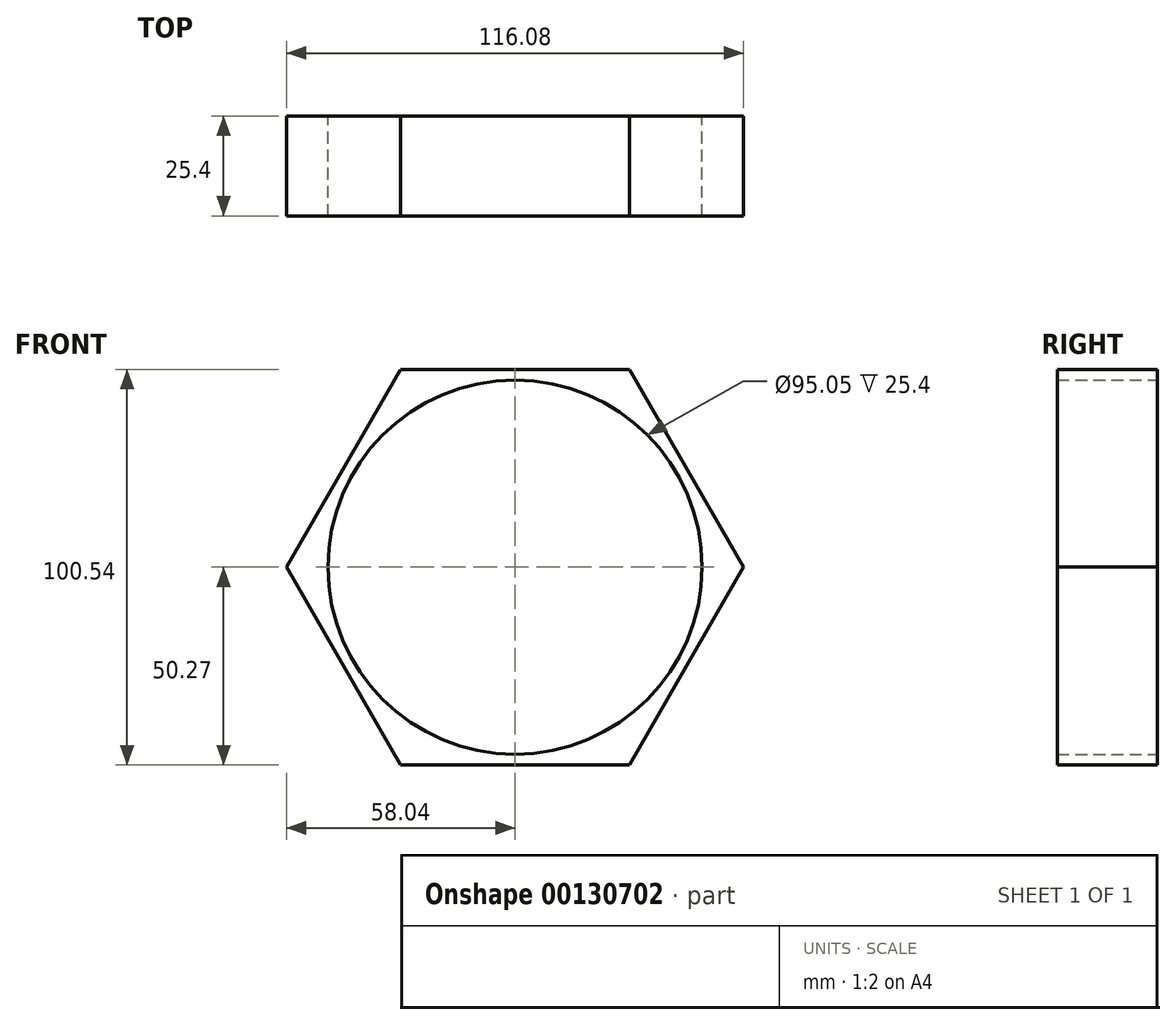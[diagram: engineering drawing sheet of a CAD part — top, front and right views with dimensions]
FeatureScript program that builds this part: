
annotation { "Feature Type Name" : "Feature", "Feature Type Description" : "" }
export const myFeature = defineFeature(function(context is Context, id is Id, definition is map)
    precondition{}
    {
        {
            var Q0;
            Q0=qCreatedBy(makeId("Front.planeOp"),FACE);
            var sketch = newSketch(context, id + "F0", { "sketchPlane" : qUnion([Q0])});
            skCircle(sketch, "E0.cCircle", {"center": v(0, 0) * mm, "radius": 50.27 * mm, "construction": true});
            skLineSegment(sketch, "E0.0", {"start": v(-29.02, 50.27) * mm, "end": v(29.02, 50.27) * mm});
            skLineSegment(sketch, "E0.1", {"start": v(29.02, 50.27) * mm, "end": v(58.04, 0) * mm});
            skLineSegment(sketch, "E0.2", {"start": v(58.04, 0) * mm, "end": v(29.02, -50.27) * mm});
            skLineSegment(sketch, "E0.3", {"start": v(29.02, -50.27) * mm, "end": v(-29.02, -50.27) * mm});
            skLineSegment(sketch, "E0.4", {"start": v(-29.02, -50.27) * mm, "end": v(-58.04, 0) * mm});
            skLineSegment(sketch, "E0.5", {"start": v(-58.04, 0) * mm, "end": v(-29.02, 50.27) * mm});
            skPoint(sketch, "E0.0.midPoint", {"position": v(0, 50.27) * mm});
            skSolve(sketch);
        }
        {
            var Q0;
            Q0=makeQuery(id+"F0.imprint","IMPRINT",FACE,{"disambiguationData":[TD([[makeQuery(id+"F0.imprint","IMPRINT",EDGE,{"derivedFrom":sQuery(id+"F0.wireOp",EDGE,"E0.0")}),-1.0]])]});
            extrude(context, id + "F1", {"entities" : qUnion([Q0]), "depth" : 25.4 * mm});
        }
        {
            var Q0;
            Q0=makeQuery(id+"F1.opExtrude","CAP_FACE",FACE,{"disambiguationData":[OSD([sQuery(id+"F0.wireOp",EDGE,"E0.0"),sQuery(id+"F0.wireOp",EDGE,"E0.1"),sQuery(id+"F0.wireOp",EDGE,"E0.2"),sQuery(id+"F0.wireOp",EDGE,"E0.3"),sQuery(id+"F0.wireOp",EDGE,"E0.4"),sQuery(id+"F0.wireOp",EDGE,"E0.5")])],"isStart":true});
            var sketch = newSketch(context, id + "F2", { "sketchPlane" : qUnion([Q0])});
            skCircle(sketch, "E1", {"center": v(0, 0) * mm, "radius": 48.43 * mm});
            skSolve(sketch);
        }
        {
            var Q0;
            Q0=makeQuery(id+"F2.imprint","IMPRINT",FACE,{"disambiguationData":[TD([[makeQuery(id+"F2.imprint","IMPRINT",EDGE,{"derivedFrom":sQuery(id+"F2.wireOp",EDGE,"E1")}),1.0]])]});
            extrude(context, id + "F3", {"entities" : qUnion([Q0]), "operationType" : NewBodyOperationType.ADD, "oppositeDirection" : true, "depth" : 1.19 * mm});
        }
        {
            var Q0;
            Q0=makeQuery(id+"F1.opExtrude","CAP_FACE",FACE,{"disambiguationData":[OSD([sQuery(id+"F0.wireOp",EDGE,"E0.0"),sQuery(id+"F0.wireOp",EDGE,"E0.1"),sQuery(id+"F0.wireOp",EDGE,"E0.2"),sQuery(id+"F0.wireOp",EDGE,"E0.3"),sQuery(id+"F0.wireOp",EDGE,"E0.4"),sQuery(id+"F0.wireOp",EDGE,"E0.5")])],"isStart":true});
            var sketch = newSketch(context, id + "F4", { "sketchPlane" : qUnion([Q0])});
            skCircle(sketch, "E2", {"center": v(0, 0) * mm, "radius": 47.53 * mm});
            skSolve(sketch);
        }
        {
            var Q0;
            Q0=makeQuery(id+"F4.imprint","IMPRINT",FACE,{"disambiguationData":[TD([[makeQuery(id+"F4.imprint","IMPRINT",EDGE,{"derivedFrom":sQuery(id+"F4.wireOp",EDGE,"E2")}),1.0]])]});
            extrude(context, id + "F5", {"entities" : qUnion([Q0]), "operationType" : NewBodyOperationType.REMOVE, "endBound" : BoundingType.SYMMETRIC, "oppositeDirection" : true, "depth" : 127 * mm});
        }
    });
